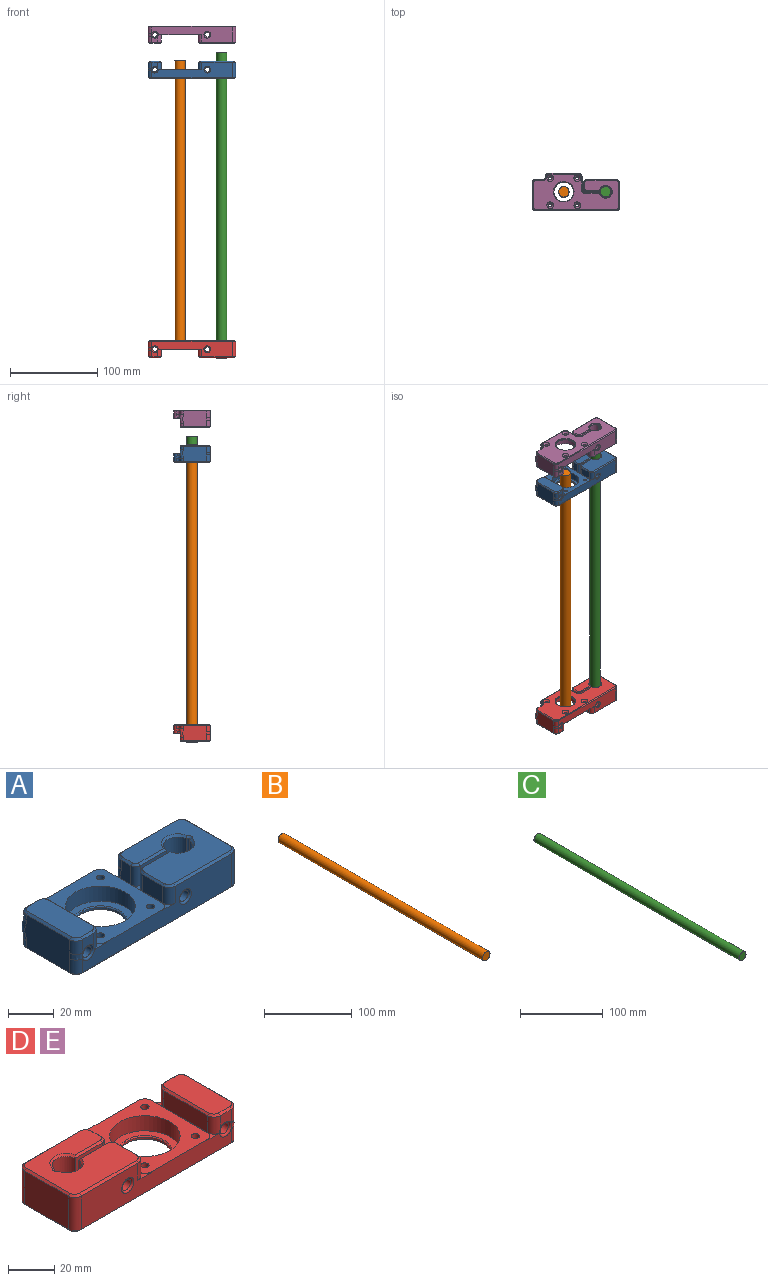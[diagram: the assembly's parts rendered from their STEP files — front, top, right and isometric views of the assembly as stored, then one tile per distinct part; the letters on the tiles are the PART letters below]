
ASSEMBLY  parts=5 mates=7
PART A: 121 faces, bbox 100.1x42.3x19.8 mm
  f0: plane 7.22x6.7mm, normal (0,-1,0), area 36.7mm2, adj f39,f48,f61,f99
  f1: plane 6.7x3.46mm, normal (0,1,0), area 18.2mm2, adj f38,f44,f47,f94
  f2: cylinder r=15.3mm len=30.6mm, axis (0,0,1), area 769.1mm2, adj f13,f14
  f3: plane 92x17.7mm, normal (0,-1,0), area 1057.3mm2, adj f13,f23,f33,f39,f43,f49,f50,f52
  f4: plane 26.7x17.7mm, normal (1,0,0), area 472.6mm2, adj f51,f62,f82,f109
  f5: plane 17.7x16.25mm, normal (0,-1,0), area 242.2mm2, adj f18,f42,f63,f70,f104
  f6: plane 27.86x17.7mm, normal (-1,0,0), area 478.2mm2, adj f45,f46,f47,f59,f60,f61,f90,f98
  f7: plane 98x40mm, normal (0,0,-1), area 2591mm2, adj f69,f70,f71,f72,f73,f74,f75,f76
  f8: cylinder r=11.25mm len=22.5mm, axis (0,0,-1), area 70.7mm2, adj f68,f69
  f9: plane 34x9mm, normal (0,1,0), area 306mm2, adj f13,f57,f58,f85
  f10: plane 34x1.34mm, normal (-1,0,0), area 10.3mm2, adj f13,f33,f49,f58,f67
  f11: plane 17.7x6.17mm, normal (-1,0,0), area 106.2mm2, adj f54,f55,f56,f63,f74,f101
  f12: plane 34x9mm, normal (1,0,0), area 132.4mm2, adj f13,f23,f50,f53,f57,f81
  f13: plane 42x42mm, normal (0,0,1), area 974.1mm2, adj f2,f3,f9,f10,f12,f34,f35,f36
  f14: plane 30.6x30.6mm, normal (0,0,1), area 301.7mm2, adj f2,f68
  f15: cylinder r=2.8mm len=6.95mm, axis (0,1,0), area 122.3mm2, adj f25,f42
  f16: plane 40.7x32.7mm, normal (0,0,1), area 1067.7mm2, adj f101,f102,f103,f104,f105,f106,f107,f108
  f17: plane 33.5x17.7mm, normal (0,1,0), area 475.1mm2, adj f40,f51,f54,f56,f78,f105
  f18: cylinder r=6.3mm len=17.7mm, axis (0,0,-1), area 318.7mm2, adj f5,f19,f71,f106
  f19: cylinder r=1.05mm len=17.7mm, axis (0,0,-1), area 50.7mm2, adj f18,f20,f73,f108
  f20: cylinder r=6.3mm len=17.7mm, axis (0,0,-1), area 313.4mm2, adj f19,f21,f75,f110
  f21: plane 17.7x16.79mm, normal (0,1,0), area 249.1mm2, adj f20,f23,f41,f53,f64,f77,f112
  f22: plane 11.95x9mm, normal (-1,0,0), area 107.5mm2, adj f23,f52,f64,f116
  f23: plane 23.95x8.3mm, normal (0,0,1), area 19.7mm2, adj f3,f12,f21,f22,f50,f52,f53,f64
  f24: cylinder r=2.8mm len=17.95mm, axis (0,1,0), area 315.8mm2, adj f41,f43
  f25: plane 10.6x10.6mm, normal (0,1,0), area 63.6mm2, adj f15,f26
  f26: cylinder r=5.3mm len=10.6mm, axis (0,1,0), area 133.2mm2, adj f25,f40
  f27: cylinder r=2.8mm len=28.7mm, axis (0,1,0), area 504.9mm2, adj f28,f39
  f28: plane 10.6x10.6mm, normal (0,1,0), area 63.6mm2, adj f27,f29
  f29: cylinder r=5.3mm len=10.6mm, axis (0,1,0), area 133.2mm2, adj f28,f38
  f30: plane 32.7x12.7mm, normal (0,0,1), area 407.6mm2, adj f93,f94,f95,f96,f97,f98,f99,f100
  f31: plane 26.7x9mm, normal (1,0,0), area 240.3mm2, adj f33,f44,f48,f95
  f32: plane 7.03x3.78mm, normal (0,1,0), area 21.4mm2, adj f38,f45,f65,f91
  f33: plane 37.91x7.97mm, normal (0,0,1), area 21.6mm2, adj f3,f10,f31,f38,f39,f44,f48,f49
  f34: cylinder r=1.8mm len=8mm, axis (0,0,-1), area 90.5mm2, adj f13,f120
  f35: cylinder r=1.8mm len=8mm, axis (0,0,-1), area 90.5mm2, adj f13,f119
  f36: cylinder r=1.8mm len=8mm, axis (0,0,-1), area 90.5mm2, adj f13,f118
  f37: cylinder r=1.8mm len=8mm, axis (0,0,-1), area 90.5mm2, adj f13,f117
  f38: torus R=6.3mm, axis (0,-1,0), area 48.5mm2, adj f1,f29,f32,f33,f44,f46,f66,f67
  f39: torus R=3.8mm, axis (0,-1,0), area 30.9mm2, adj f0,f3,f27,f33,f48,f60
  f40: torus R=6.3mm, axis (0,1,0), area 55.9mm2, adj f17,f26,f55
  f41: torus R=3.8mm, axis (0,1,0), area 31.2mm2, adj f21,f24
  f42: torus R=3.8mm, axis (0,1,0), area 31.2mm2, adj f5,f15
  f43: torus R=3.8mm, axis (0,-1,0), area 31.2mm2, adj f3,f24
  f44: cylinder r=4mm len=9mm, axis (0,0,-1), area 47.7mm2, adj f1,f31,f33,f38,f93
  f45: cylinder r=4mm len=4mm, axis (0,0,1), area 23.6mm2, adj f6,f32,f46,f92
  f46: bspline ~10.48x4mm, area 45mm2, adj f6,f38,f45,f47
  f47: cylinder r=4mm len=4mm, axis (0,0,1), area 21.8mm2, adj f1,f6,f46,f96
  f48: cylinder r=4mm len=9mm, axis (0,0,-1), area 55.9mm2, adj f0,f31,f33,f39,f97
  f49: cylinder r=4mm len=4mm, axis (0,0,-1), area 1.9mm2, adj f3,f10,f13,f33
  f50: cylinder r=4mm len=4mm, axis (0,0,-1), area 1.9mm2, adj f3,f12,f13,f23
  f51: cylinder r=4mm len=17.7mm, axis (0,0,1), area 111.2mm2, adj f4,f17,f80,f107
  f52: cylinder r=4mm len=9mm, axis (0,0,1), area 56.5mm2, adj f3,f22,f23,f115
  f53: cylinder r=4mm len=8.7mm, axis (0,0,-1), area 54.7mm2, adj f12,f21,f23,f79
  f54: cylinder r=4mm len=5.17mm, axis (0,0,1), area 32.5mm2, adj f11,f17,f55,f76
  f55: bspline ~8.61x4.36mm, area 41.4mm2, adj f11,f40,f54,f56
  f56: cylinder r=4mm len=4.87mm, axis (0,0,1), area 30.6mm2, adj f11,f17,f55,f103
  f57: cylinder r=4mm len=9mm, axis (0,0,-1), area 56.5mm2, adj f9,f12,f13,f83
  f58: cylinder r=4mm len=9mm, axis (0,0,-1), area 54.5mm2, adj f9,f10,f13,f65,f66,f87
  f59: cylinder r=4mm len=7.52mm, axis (0,0,-1), area 47.3mm2, adj f3,f6,f60,f88
  f60: bspline ~4.24x4.22mm, area 18mm2, adj f6,f39,f59,f61
  f61: cylinder r=4mm len=7.22mm, axis (0,0,-1), area 45.4mm2, adj f0,f6,f60,f100
  f62: cylinder r=4mm len=17.7mm, axis (0,0,1), area 111.2mm2, adj f3,f4,f84,f111
  f63: cylinder r=3mm len=17.7mm, axis (0,0,-1), area 83.4mm2, adj f5,f11,f72,f102
  f64: cylinder r=4mm len=9mm, axis (0,0,-1), area 56.5mm2, adj f21,f22,f23,f114
  f65: cylinder r=4mm len=3.98mm, axis (0,0,-1), area 22.4mm2, adj f32,f58,f66,f89
  f66: bspline ~6.27x4.49mm, area 17.2mm2, adj f38,f58,f65,f67
  f67: bspline ~3.63x3.48mm, area 5.8mm2, adj f10,f33,f38,f66
  f68: cone r=11.25mm half-angle=45deg, axis (0,0,1), area 51.1mm2, adj f8,f14
  f69: cone r=11.75mm half-angle=45deg, axis (0,0,-1), area 51.1mm2, adj f7,f8
  f70: plane 16.3x1.05mm, normal (0,-0.71,-0.71), area 22.4mm2, adj f5,f7,f71,f72
  f71: cone r=7.3mm half-angle=45deg, axis (0,0,-1), area 26.5mm2, adj f7,f18,f70,f73
  f72: cone r=2mm half-angle=45deg, axis (0,0,1), area 5.6mm2, adj f7,f63,f70,f74
  f73: cone r=2.05mm half-angle=45deg, axis (0,0,-1), area 5.1mm2, adj f7,f19,f71,f75
  f74: plane 5.95x1mm, normal (-0.71,0,-0.71), area 8.4mm2, adj f7,f11,f72,f76
  f75: cone r=7.3mm half-angle=45deg, axis (0,0,-1), area 26.1mm2, adj f7,f20,f73,f77
  f76: cone r=3mm half-angle=45deg, axis (0,0,1), area 7.8mm2, adj f7,f54,f74,f78
  f77: plane 16.84x1.05mm, normal (0,0.71,-0.71), area 23.2mm2, adj f7,f21,f75,f79
  f78: plane 33.5x1mm, normal (0,0.71,-0.71), area 47.4mm2, adj f7,f17,f76,f80
  f79: cone r=5mm half-angle=45deg, axis (0,0,-1), area 10mm2, adj f7,f53,f77,f81
  f80: cone r=3mm half-angle=45deg, axis (0,0,1), area 7.8mm2, adj f7,f51,f78,f82
  f81: plane 14.05x1mm, normal (0.71,0,-0.71), area 19.9mm2, adj f7,f12,f79,f83
  f82: plane 26.7x1mm, normal (0.71,0,-0.71), area 37.8mm2, adj f4,f7,f80,f84
  f83: cone r=3mm half-angle=45deg, axis (0,0,1), area 7.8mm2, adj f7,f57,f81,f85
  f84: cone r=3mm half-angle=45deg, axis (0,0,1), area 7.8mm2, adj f7,f62,f82,f86
  f85: plane 34x1mm, normal (0,0.71,-0.71), area 48.1mm2, adj f7,f9,f83,f87
  f86: plane 92x1mm, normal (0,-0.71,-0.71), area 130.1mm2, adj f3,f7,f84,f88
  f87: cone r=3mm half-angle=45deg, axis (0,0,1), area 7.3mm2, adj f7,f58,f85,f89
  f88: cone r=3mm half-angle=45deg, axis (0,0,1), area 7.8mm2, adj f7,f59,f86,f90
  f89: cone r=5mm half-angle=45deg, axis (0,0,-1), area 9.4mm2, adj f7,f65,f87,f91
  f90: plane 26.7x1mm, normal (-0.71,0,-0.71), area 37.8mm2, adj f6,f7,f88,f92
  f91: plane 7.03x1mm, normal (0,0.71,-0.71), area 9.9mm2, adj f7,f32,f89,f92
  f92: cone r=3mm half-angle=45deg, axis (0,0,1), area 7.8mm2, adj f7,f45,f90,f91
  f93: cone r=3mm half-angle=45deg, axis (0,0,-1), area 7.8mm2, adj f30,f44,f94,f95
  f94: plane 6.7x1mm, normal (0,0.71,0.71), area 9.5mm2, adj f1,f30,f93,f96
  f95: plane 26.7x1mm, normal (0.71,0,0.71), area 37.8mm2, adj f30,f31,f93,f97
  f96: cone r=3mm half-angle=45deg, axis (0,0,-1), area 7.8mm2, adj f30,f47,f94,f98
  f97: cone r=3mm half-angle=45deg, axis (0,0,-1), area 7.8mm2, adj f30,f48,f95,f99
  f98: plane 26.7x1mm, normal (-0.71,0,0.71), area 37.8mm2, adj f6,f30,f96,f100
  f99: plane 6.7x1mm, normal (0,-0.71,0.71), area 9.5mm2, adj f0,f30,f97,f100
  f100: cone r=3mm half-angle=45deg, axis (0,0,-1), area 7.8mm2, adj f30,f61,f98,f99
  f101: plane 5.95x1mm, normal (-0.71,0,0.71), area 8.4mm2, adj f11,f16,f102,f103
  f102: cone r=2mm half-angle=45deg, axis (0,0,-1), area 5.6mm2, adj f16,f63,f101,f104
  f103: cone r=3mm half-angle=45deg, axis (0,0,-1), area 7.8mm2, adj f16,f56,f101,f105
  f104: plane 16.3x1.05mm, normal (0,-0.71,0.71), area 22.4mm2, adj f5,f16,f102,f106
  f105: plane 33.5x1mm, normal (0,0.71,0.71), area 47.4mm2, adj f16,f17,f103,f107
  f106: cone r=6.3mm half-angle=45deg, axis (0,0,1), area 26.5mm2, adj f16,f18,f104,f108
  f107: cone r=3mm half-angle=45deg, axis (0,0,-1), area 7.8mm2, adj f16,f51,f105,f109
  f108: cone r=1.05mm half-angle=45deg, axis (0,0,1), area 5.1mm2, adj f16,f19,f106,f110
  f109: plane 26.7x1mm, normal (0.71,0,0.71), area 37.8mm2, adj f4,f16,f107,f111
  f110: cone r=6.3mm half-angle=45deg, axis (0,0,1), area 26.1mm2, adj f16,f20,f108,f112
  f111: cone r=3mm half-angle=45deg, axis (0,0,-1), area 7.8mm2, adj f16,f62,f109,f113
  f112: plane 16.54x1.05mm, normal (0,0.71,0.71), area 22.7mm2, adj f16,f21,f110,f114
  f113: plane 34.7x1mm, normal (0,-0.71,0.71), area 49.1mm2, adj f3,f16,f111,f115
  f114: cone r=3mm half-angle=45deg, axis (0,0,-1), area 7.8mm2, adj f16,f64,f112,f116
  f115: cone r=3mm half-angle=45deg, axis (0,0,-1), area 7.8mm2, adj f16,f52,f113,f116
  f116: plane 11.95x1mm, normal (-0.71,0,0.71), area 16.9mm2, adj f16,f22,f114,f115
  f117: cone r=3.8mm half-angle=45deg, axis (0,0,-1), area 49.8mm2, adj f7,f37
  f118: cone r=3.8mm half-angle=45deg, axis (0,0,-1), area 49.8mm2, adj f7,f36
  f119: cone r=3.8mm half-angle=45deg, axis (0,0,-1), area 49.8mm2, adj f7,f35
  f120: cone r=3.8mm half-angle=45deg, axis (0,0,-1), area 49.8mm2, adj f7,f34
PART B: 3 faces, bbox 12x330x12 mm
  f0: cylinder r=6mm len=330mm, axis (0,1,0), area 12440.7mm2, adj f1,f2
  f1: plane 12x12mm, normal (0,-1,0), area 113.1mm2, adj f0
  f2: plane 12x12mm, normal (0,1,0), area 113.1mm2, adj f0
PART C: 3 faces, bbox 12x350x12 mm
  f0: cylinder r=6mm len=350mm, axis (0,1,0), area 13194.7mm2, adj f1,f2
  f1: plane 12x12mm, normal (0,-1,0), area 113.1mm2, adj f0
  f2: plane 12x12mm, normal (0,1,0), area 113.1mm2, adj f0
PART D: 121 faces, bbox 100.1x42.7x19.8 mm
  f0: plane 6.7x3.46mm, normal (0,1,0), area 18.2mm2, adj f41,f47,f54,f94
  f1: plane 7.22x6.7mm, normal (0,-1,0), area 36.7mm2, adj f42,f45,f62,f99
  f2: cylinder r=15.3mm len=30.6mm, axis (0,0,1), area 769.1mm2, adj f13,f14
  f3: plane 92x17.7mm, normal (0,-1,0), area 1057.3mm2, adj f13,f23,f33,f38,f42,f46,f55,f56
  f4: plane 26.7x17.7mm, normal (-1,0,0), area 472.6mm2, adj f48,f59,f82,f109
  f5: plane 17.7x16.25mm, normal (0,-1,0), area 242.2mm2, adj f18,f39,f63,f70,f104
  f6: plane 27.86x17.7mm, normal (1,0,0), area 478.2mm2, adj f52,f53,f54,f60,f61,f62,f90,f98
  f7: plane 98x40mm, normal (0,0,-1), area 2591mm2, adj f69,f70,f71,f72,f73,f74,f75,f76
  f8: cylinder r=11.25mm len=22.5mm, axis (0,0,-1), area 70.7mm2, adj f68,f69
  f9: plane 34x9mm, normal (0,1,0), area 306mm2, adj f13,f57,f58,f85
  f10: plane 34x1.34mm, normal (1,0,0), area 10.3mm2, adj f13,f33,f55,f58,f67
  f11: plane 17.7x6.17mm, normal (1,0,0), area 106.2mm2, adj f49,f50,f51,f63,f74,f101
  f12: plane 34x9mm, normal (-1,0,0), area 132.4mm2, adj f13,f23,f44,f56,f57,f81
  f13: plane 42x42mm, normal (0,0,1), area 974.1mm2, adj f2,f3,f9,f10,f12,f34,f35,f36
  f14: plane 30.6x30.6mm, normal (0,0,1), area 301.7mm2, adj f2,f68
  f15: cylinder r=2.8mm len=6.95mm, axis (0,1,0), area 122.3mm2, adj f25,f39
  f16: plane 40.7x32.7mm, normal (0,0,1), area 1067.7mm2, adj f101,f102,f103,f104,f105,f106,f107,f108
  f17: plane 33.5x17.7mm, normal (0,1,0), area 475.1mm2, adj f40,f48,f49,f51,f78,f105
  f18: cylinder r=6.3mm len=17.7mm, axis (0,0,-1), area 318.7mm2, adj f5,f19,f71,f106
  f19: cylinder r=1.05mm len=17.7mm, axis (0,0,-1), area 50.7mm2, adj f18,f20,f73,f108
  f20: cylinder r=6.3mm len=17.7mm, axis (0,0,-1), area 313.4mm2, adj f19,f21,f75,f110
  f21: plane 17.7x16.79mm, normal (0,1,0), area 249.1mm2, adj f20,f23,f43,f44,f64,f77,f112
  f22: plane 11.95x9mm, normal (1,0,0), area 107.5mm2, adj f23,f46,f64,f116
  f23: plane 23.95x8.3mm, normal (0,0,1), area 19.7mm2, adj f3,f12,f21,f22,f44,f46,f56,f64
  f24: cylinder r=2.8mm len=17.95mm, axis (0,1,0), area 315.8mm2, adj f38,f43
  f25: plane 10.6x10.6mm, normal (0,1,0), area 63.6mm2, adj f15,f26
  f26: cylinder r=5.3mm len=10.6mm, axis (0,1,0), area 133.2mm2, adj f25,f40
  f27: cylinder r=2.8mm len=28.7mm, axis (0,1,0), area 504.9mm2, adj f28,f42
  f28: plane 10.6x10.6mm, normal (0,1,0), area 63.6mm2, adj f27,f29
  f29: cylinder r=5.3mm len=10.6mm, axis (0,1,0), area 133.2mm2, adj f28,f41
  f30: plane 32.7x12.7mm, normal (0,0,1), area 407.6mm2, adj f93,f94,f95,f96,f97,f98,f99,f100
  f31: plane 26.7x9mm, normal (-1,0,0), area 240.3mm2, adj f33,f45,f47,f95
  f32: plane 7.03x3.78mm, normal (0,1,0), area 21.4mm2, adj f41,f52,f65,f91
  f33: plane 37.91x7.97mm, normal (0,0,1), area 21.6mm2, adj f3,f10,f31,f41,f42,f45,f47,f55
  f34: cylinder r=1.8mm len=8mm, axis (0,0,-1), area 90.5mm2, adj f13,f120
  f35: cylinder r=1.8mm len=8mm, axis (0,0,-1), area 90.5mm2, adj f13,f119
  f36: cylinder r=1.8mm len=8mm, axis (0,0,-1), area 90.5mm2, adj f13,f118
  f37: cylinder r=1.8mm len=8mm, axis (0,0,-1), area 90.5mm2, adj f13,f117
  f38: torus R=3.8mm, axis (0,-1,0), area 31.2mm2, adj f3,f24
  f39: torus R=3.8mm, axis (0,1,0), area 31.2mm2, adj f5,f15
  f40: torus R=6.3mm, axis (0,1,0), area 55.9mm2, adj f17,f26,f50
  f41: torus R=6.3mm, axis (0,-1,0), area 48.5mm2, adj f0,f29,f32,f33,f47,f53,f66,f67
  f42: torus R=3.8mm, axis (0,-1,0), area 30.9mm2, adj f1,f3,f27,f33,f45,f61
  f43: torus R=3.8mm, axis (0,1,0), area 31.2mm2, adj f21,f24
  f44: cylinder r=4mm len=8.7mm, axis (0,0,-1), area 54.7mm2, adj f12,f21,f23,f79
  f45: cylinder r=4mm len=9mm, axis (0,0,-1), area 55.9mm2, adj f1,f31,f33,f42,f97
  f46: cylinder r=4mm len=9mm, axis (0,0,1), area 56.5mm2, adj f3,f22,f23,f115
  f47: cylinder r=4mm len=9mm, axis (0,0,-1), area 47.7mm2, adj f0,f31,f33,f41,f93
  f48: cylinder r=4mm len=17.7mm, axis (0,0,1), area 111.2mm2, adj f4,f17,f80,f107
  f49: cylinder r=4mm len=5.17mm, axis (0,0,1), area 32.5mm2, adj f11,f17,f50,f76
  f50: bspline ~8.61x4.36mm, area 41.4mm2, adj f11,f40,f49,f51
  f51: cylinder r=4mm len=4.87mm, axis (0,0,1), area 30.6mm2, adj f11,f17,f50,f103
  f52: cylinder r=4mm len=4mm, axis (0,0,1), area 23.6mm2, adj f6,f32,f53,f92
  f53: bspline ~10.48x4mm, area 45mm2, adj f6,f41,f52,f54
  f54: cylinder r=4mm len=4mm, axis (0,0,1), area 21.8mm2, adj f0,f6,f53,f96
  f55: cylinder r=4mm len=4mm, axis (0,0,-1), area 1.9mm2, adj f3,f10,f13,f33
  f56: cylinder r=4mm len=4mm, axis (0,0,-1), area 1.9mm2, adj f3,f12,f13,f23
  f57: cylinder r=4mm len=9mm, axis (0,0,-1), area 56.5mm2, adj f9,f12,f13,f83
  f58: cylinder r=4mm len=9mm, axis (0,0,-1), area 54.5mm2, adj f9,f10,f13,f65,f66,f87
  f59: cylinder r=4mm len=17.7mm, axis (0,0,1), area 111.2mm2, adj f3,f4,f84,f111
  f60: cylinder r=4mm len=7.52mm, axis (0,0,-1), area 47.3mm2, adj f3,f6,f61,f88
  f61: bspline ~4.81x4.68mm, area 18mm2, adj f6,f42,f60,f62
  f62: cylinder r=4mm len=7.22mm, axis (0,0,-1), area 45.4mm2, adj f1,f6,f61,f100
  f63: cylinder r=3mm len=17.7mm, axis (0,0,-1), area 83.4mm2, adj f5,f11,f72,f102
  f64: cylinder r=4mm len=9mm, axis (0,0,-1), area 56.5mm2, adj f21,f22,f23,f114
  f65: cylinder r=4mm len=3.98mm, axis (0,0,-1), area 22.4mm2, adj f32,f58,f66,f89
  f66: bspline ~6.27x4.49mm, area 17.2mm2, adj f41,f58,f65,f67
  f67: bspline ~3.63x3.48mm, area 5.8mm2, adj f10,f33,f41,f66
  f68: cone r=11.25mm half-angle=45deg, axis (0,0,1), area 51.1mm2, adj f8,f14
  f69: cone r=11.75mm half-angle=45deg, axis (0,0,-1), area 51.1mm2, adj f7,f8
  f70: plane 16.3x1.05mm, normal (0,-0.71,-0.71), area 22.4mm2, adj f5,f7,f71,f72
  f71: cone r=7.3mm half-angle=45deg, axis (0,0,-1), area 26.5mm2, adj f7,f18,f70,f73
  f72: cone r=2mm half-angle=45deg, axis (0,0,1), area 5.6mm2, adj f7,f63,f70,f74
  f73: cone r=2.05mm half-angle=45deg, axis (0,0,-1), area 5.1mm2, adj f7,f19,f71,f75
  f74: plane 5.95x1mm, normal (0.71,0,-0.71), area 8.4mm2, adj f7,f11,f72,f76
  f75: cone r=7.3mm half-angle=45deg, axis (0,0,-1), area 26.1mm2, adj f7,f20,f73,f77
  f76: cone r=3mm half-angle=45deg, axis (0,0,1), area 7.8mm2, adj f7,f49,f74,f78
  f77: plane 16.84x1.05mm, normal (0,0.71,-0.71), area 23.2mm2, adj f7,f21,f75,f79
  f78: plane 33.5x1mm, normal (0,0.71,-0.71), area 47.4mm2, adj f7,f17,f76,f80
  f79: cone r=5mm half-angle=45deg, axis (0,0,-1), area 10mm2, adj f7,f44,f77,f81
  f80: cone r=3mm half-angle=45deg, axis (0,0,1), area 7.8mm2, adj f7,f48,f78,f82
  f81: plane 14.05x1mm, normal (-0.71,0,-0.71), area 19.9mm2, adj f7,f12,f79,f83
  f82: plane 26.7x1mm, normal (-0.71,0,-0.71), area 37.8mm2, adj f4,f7,f80,f84
  f83: cone r=3mm half-angle=45deg, axis (0,0,1), area 7.8mm2, adj f7,f57,f81,f85
  f84: cone r=3mm half-angle=45deg, axis (0,0,1), area 7.8mm2, adj f7,f59,f82,f86
  f85: plane 34x1mm, normal (0,0.71,-0.71), area 48.1mm2, adj f7,f9,f83,f87
  f86: plane 92x1mm, normal (0,-0.71,-0.71), area 130.1mm2, adj f3,f7,f84,f88
  f87: cone r=3mm half-angle=45deg, axis (0,0,1), area 7.3mm2, adj f7,f58,f85,f89
  f88: cone r=3mm half-angle=45deg, axis (0,0,1), area 7.8mm2, adj f7,f60,f86,f90
  f89: cone r=5mm half-angle=45deg, axis (0,0,-1), area 9.4mm2, adj f7,f65,f87,f91
  f90: plane 26.7x1mm, normal (0.71,0,-0.71), area 37.8mm2, adj f6,f7,f88,f92
  f91: plane 7.03x1mm, normal (0,0.71,-0.71), area 9.9mm2, adj f7,f32,f89,f92
  f92: cone r=3mm half-angle=45deg, axis (0,0,1), area 7.8mm2, adj f7,f52,f90,f91
  f93: cone r=3mm half-angle=45deg, axis (0,0,-1), area 7.8mm2, adj f30,f47,f94,f95
  f94: plane 6.7x1mm, normal (0,0.71,0.71), area 9.5mm2, adj f0,f30,f93,f96
  f95: plane 26.7x1mm, normal (-0.71,0,0.71), area 37.8mm2, adj f30,f31,f93,f97
  f96: cone r=3mm half-angle=45deg, axis (0,0,-1), area 7.8mm2, adj f30,f54,f94,f98
  f97: cone r=3mm half-angle=45deg, axis (0,0,-1), area 7.8mm2, adj f30,f45,f95,f99
  f98: plane 26.7x1mm, normal (0.71,0,0.71), area 37.8mm2, adj f6,f30,f96,f100
  f99: plane 6.7x1mm, normal (0,-0.71,0.71), area 9.5mm2, adj f1,f30,f97,f100
  f100: cone r=3mm half-angle=45deg, axis (0,0,-1), area 7.8mm2, adj f30,f62,f98,f99
  f101: plane 5.95x1mm, normal (0.71,0,0.71), area 8.4mm2, adj f11,f16,f102,f103
  f102: cone r=2mm half-angle=45deg, axis (0,0,-1), area 5.6mm2, adj f16,f63,f101,f104
  f103: cone r=3mm half-angle=45deg, axis (0,0,-1), area 7.8mm2, adj f16,f51,f101,f105
  f104: plane 16.3x1.05mm, normal (0,-0.71,0.71), area 22.4mm2, adj f5,f16,f102,f106
  f105: plane 33.5x1mm, normal (0,0.71,0.71), area 47.4mm2, adj f16,f17,f103,f107
  f106: cone r=6.3mm half-angle=45deg, axis (0,0,1), area 26.5mm2, adj f16,f18,f104,f108
  f107: cone r=3mm half-angle=45deg, axis (0,0,-1), area 7.8mm2, adj f16,f48,f105,f109
  f108: cone r=1.05mm half-angle=45deg, axis (0,0,1), area 5.1mm2, adj f16,f19,f106,f110
  f109: plane 26.7x1mm, normal (-0.71,0,0.71), area 37.8mm2, adj f4,f16,f107,f111
  f110: cone r=6.3mm half-angle=45deg, axis (0,0,1), area 26.1mm2, adj f16,f20,f108,f112
  f111: cone r=3mm half-angle=45deg, axis (0,0,-1), area 7.8mm2, adj f16,f59,f109,f113
  f112: plane 16.54x1.05mm, normal (0,0.71,0.71), area 22.7mm2, adj f16,f21,f110,f114
  f113: plane 34.7x1mm, normal (0,-0.71,0.71), area 49.1mm2, adj f3,f16,f111,f115
  f114: cone r=3mm half-angle=45deg, axis (0,0,-1), area 7.8mm2, adj f16,f64,f112,f116
  f115: cone r=3mm half-angle=45deg, axis (0,0,-1), area 7.8mm2, adj f16,f46,f113,f116
  f116: plane 11.95x1mm, normal (0.71,0,0.71), area 16.9mm2, adj f16,f22,f114,f115
  f117: cone r=3.8mm half-angle=45deg, axis (0,0,-1), area 49.8mm2, adj f7,f37
  f118: cone r=3.8mm half-angle=45deg, axis (0,0,-1), area 49.8mm2, adj f7,f36
  f119: cone r=3.8mm half-angle=45deg, axis (0,0,-1), area 49.8mm2, adj f7,f35
  f120: cone r=3.8mm half-angle=45deg, axis (0,0,-1), area 49.8mm2, adj f7,f34
PART E: same geometry as D
PLACE A at identity fixed
PLACE B rot(axis=(-1,0,0),90deg) t=(0,0,-154.7)mm
PLACE C rot(axis=(-1,0,0),90deg) t=(48,0,-155)mm
PLACE D rot(axis=(0,1,0),180deg) t=(0,0,-320)mm
PLACE E rot(axis=(0,1,0),180deg) t=(0,0,40)mm
MATE cylindrical A.f18 <-> C.f0  axis (0,0,-1) through (48,0,-9)mm
MATE planar A.f16 <-> C.f0  axis (0,0,1) through (42.81,-4.6,9.7)mm
MATE planar B.f0 <-> D.f23  axis (0,0,-1) through (0,0,-319.7)mm
MATE planar D.f3 <-> A.f3  axis (0,-1,0) through (22.39,-21,-317.75)mm
MATE cylindrical B.f0 <-> D.f2  axis (0,0,-1) through (0,0,-154.7)mm
MATE planar D.f16 <-> C.f0  axis (0,0,-1) through (33.21,1.75,-329.7)mm
MATE cylindrical D.f18 <-> C.f0  axis (0,0,1) through (48,0,-319.85)mm
